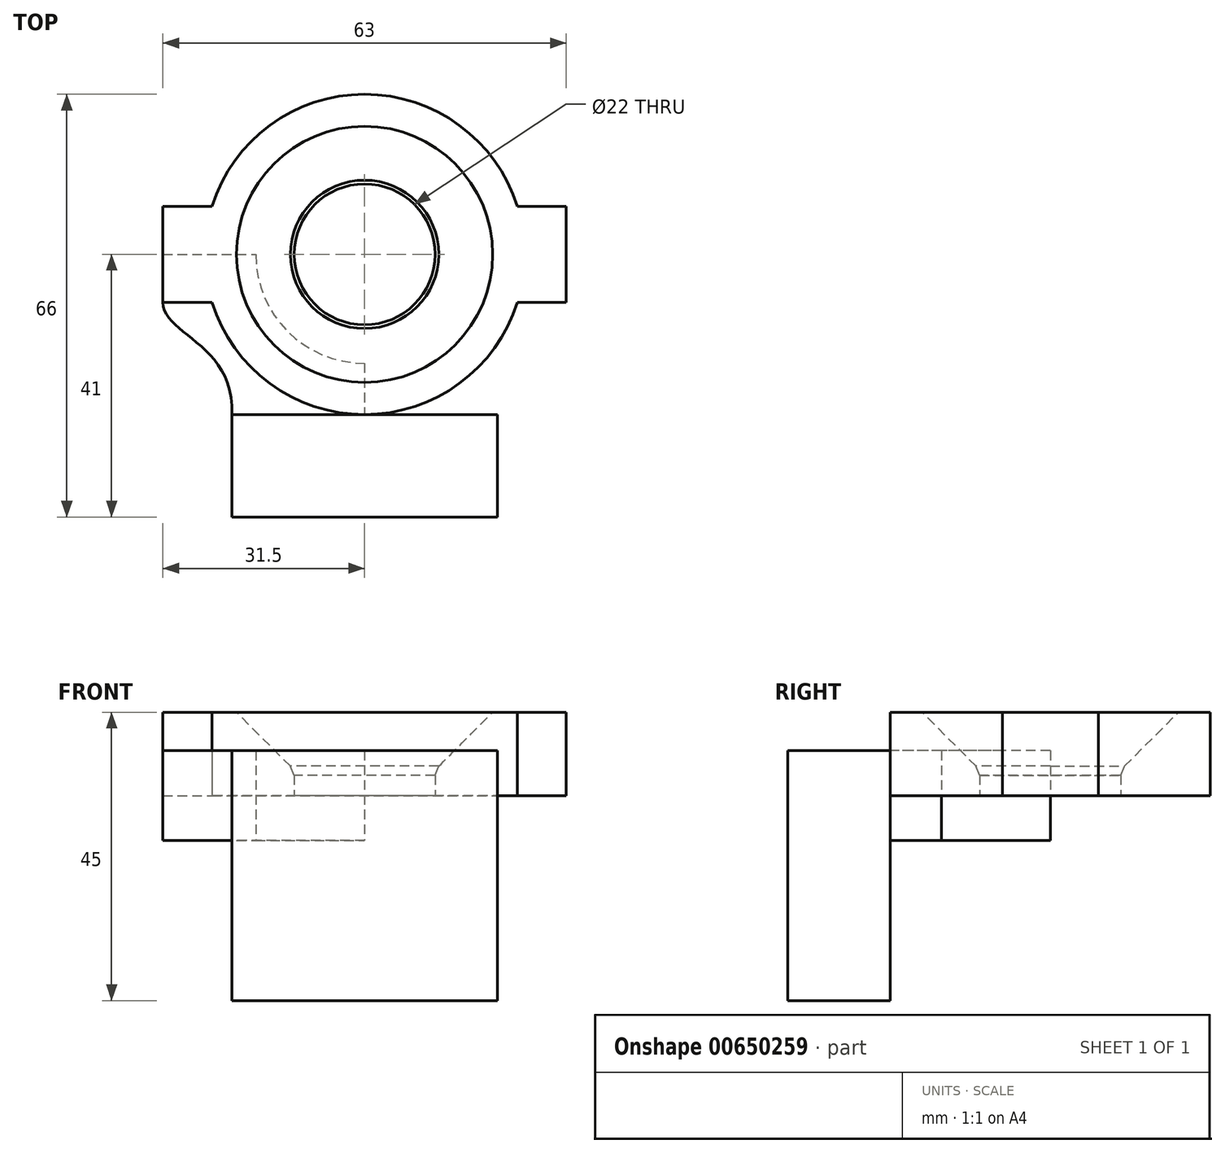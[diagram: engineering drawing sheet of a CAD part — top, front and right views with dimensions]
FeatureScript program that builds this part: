
annotation { "Feature Type Name" : "Feature", "Feature Type Description" : "" }
export const myFeature = defineFeature(function(context is Context, id is Id, definition is map)
    precondition{}
    {
        {
            var Q0;
            Q0=qCreatedBy(makeId("Top.planeOp"),FACE);
            var sketch = newSketch(context, id + "F0", { "sketchPlane" : qUnion([Q0])});
            skCircle(sketch, "E0", {"center": v(0, 0) * mm, "radius": 11 * mm});
            skCircle(sketch, "E1", {"center": v(0, 0) * mm, "radius": 25 * mm});
            skLineSegment(sketch, "E2", {"start": v(23.5, 0) * mm, "end": v(23.5, 7.5) * mm});
            skLineSegment(sketch, "E3", {"start": v(23.5, 7.5) * mm, "end": v(31.5, 7.5) * mm});
            skLineSegment(sketch, "E4", {"start": v(0, 0) * mm, "end": v(23.5, 0) * mm});
            skLineSegment(sketch, "E5", {"start": v(31.5, 7.5) * mm, "end": v(31.5, -7.5) * mm});
            skLineSegment(sketch, "E6", {"start": v(31.5, -7.5) * mm, "end": v(23.5, -7.5) * mm});
            skLineSegment(sketch, "E7", {"start": v(23.5, -7.5) * mm, "end": v(23.5, 0) * mm});
            skLineSegment(sketch, "E8", {"start": v(0, 0) * mm, "end": v(-23.5, 0) * mm});
            skLineSegment(sketch, "E9", {"start": v(-23.5, 0) * mm, "end": v(-23.5, 7.5) * mm});
            skLineSegment(sketch, "E10", {"start": v(-23.5, 7.5) * mm, "end": v(-31.5, 7.5) * mm});
            skLineSegment(sketch, "E11", {"start": v(-31.5, 7.5) * mm, "end": v(-31.5, -7.5) * mm});
            skLineSegment(sketch, "E12", {"start": v(-31.5, -7.5) * mm, "end": v(-23.5, -7.5) * mm});
            skLineSegment(sketch, "E13", {"start": v(-23.5, -7.5) * mm, "end": v(-23.5, 0) * mm});
            skSolve(sketch);
        }
        {
            var Q0;
            Q0 = qSketchRegion(id + "F0", true);
            extrude(context, id + "F1", {"entities" : qUnion([Q0]), "depth" : 13 * mm, "offsetDistance" : 25 * mm});
        }
        {
            var Q0;
            Q0=makeQuery(id+"F1.opExtrude","CAP_EDGE",EDGE,{"disambiguationData":[OSD([sQuery(id+"F0.wireOp",EDGE,"E0")])],"isStart":false});
            chamfer(context, id + "F2", {"entities" : qUnion([Q0]), "width" : 9 * mm, "tangentPropagation" : true});
        }
        {
            var Q0;
            {var subQ0=sQuery(id+"F0.wireOp",EDGE,"E0");Q0=makeQuery(id+"F2.opChamfer","BLEND_EDGE",EDGE,{"blendedFrom":[makeQuery(id+"F1.opExtrude","CAP_EDGE",EDGE,{"disambiguationData":[OSD([subQ0])],"isStart":false}),makeQuery(id+"F1.opExtrude","SWEPT_FACE",FACE,{"disambiguationData":[OSD([subQ0])]})],"blendedInto":[makeQuery(id+"F1.opExtrude","SWEPT_FACE",FACE,{"disambiguationData":[OSD([subQ0])]})]});}
            chamfer(context, id + "F3", {"entities" : qUnion([Q0]), "width" : 2 * mm, "tangentPropagation" : true});
        }
        {
            var Q0;
            Q0=qCreatedBy(makeId("Top.planeOp"),FACE);
            var sketch = newSketch(context, id + "F4", { "sketchPlane" : qUnion([Q0])});
            skLineSegment(sketch, "E14", {"start": v(0, 0) * mm, "end": v(0, -33) * mm});
            skLineSegment(sketch, "E15.bottom", {"start": v(20.75, -41) * mm, "end": v(-20.75, -41) * mm});
            skLineSegment(sketch, "E15.top", {"start": v(20.75, -25) * mm, "end": v(-20.75, -25) * mm});
            skLineSegment(sketch, "E15.left", {"start": v(20.75, -41) * mm, "end": v(20.75, -25) * mm});
            skLineSegment(sketch, "E15.right", {"start": v(-20.75, -41) * mm, "end": v(-20.75, -25) * mm});
            skPoint(sketch, "E15.middle", {"position": v(0, -33) * mm});
            skSolve(sketch);
        }
        {
            var Q0;
            Q0 = qSketchRegion(id + "F4", true);
            extrude(context, id + "F5", {"entities" : qUnion([Q0]), "operationType" : NewBodyOperationType.ADD, "depth" : 39 * mm, "offsetDistance" : 25 * mm});
        }
        {
            var Q0;
            Q0=makeQuery(id+"F5.opExtrude","SWEPT_BODY",BODY,{"disambiguationData":[OSD([sQuery(id+"F4.wireOp",EDGE,"E15.bottom"),sQuery(id+"F4.wireOp",EDGE,"E15.top"),sQuery(id+"F4.wireOp",EDGE,"E15.left"),sQuery(id+"F4.wireOp",EDGE,"E15.right")])]});
            transform(context, id + "F6", {"entities" : qUnion([Q0]), "transformType" : TransformType.TRANSLATION_3D, "dx" : 0 * mm, "dy" : 0 * mm, "dz" : -32 * mm, "makeCopy" : false});
        }
        {
            var Q0;
            Q0=qCreatedBy(makeId("Top.planeOp"),FACE);
            var sketch = newSketch(context, id + "F7", { "sketchPlane" : qUnion([Q0])});
            skLineSegment(sketch, "E16", {"start": v(0, 0) * mm, "end": v(31.5, 0) * mm});
            skLineSegment(sketch, "E17", {"start": v(0, -25) * mm, "end": v(-20.75, -25) * mm});
            skLineSegment(sketch, "E18", {"start": v(-31.5, 0) * mm, "end": v(-31.5, -7.5) * mm});
            skFitSpline(sketch, "E19", {"points": [v(-31.5, -7.5) * mm, v(-20.75, -25) * mm], "startDerivative": vector(0.3, -15.25) * mm, "endDerivative": vector(-1.77, -32.8) * mm});
            skArc(sketch, "E20", {"start": v(-17, 0) * mm, "mid": v(-12.02, -12.02) * mm, "end": v(0, -17) * mm});
            skLineSegment(sketch, "E21", {"start": v(-31.5, 0) * mm, "end": v(-17, 0) * mm});
            skLineSegment(sketch, "E22", {"start": v(0, -17) * mm, "end": v(0, -25) * mm});
            skSolve(sketch);
        }
        {
            var Q0;
            Q0 = qSketchRegion(id + "F7", true);
            extrude(context, id + "F8", {"entities" : qUnion([Q0]), "endBound" : BoundingType.SYMMETRIC, "depth" : 14 * mm, "offsetDistance" : 25 * mm});
        }
    });
